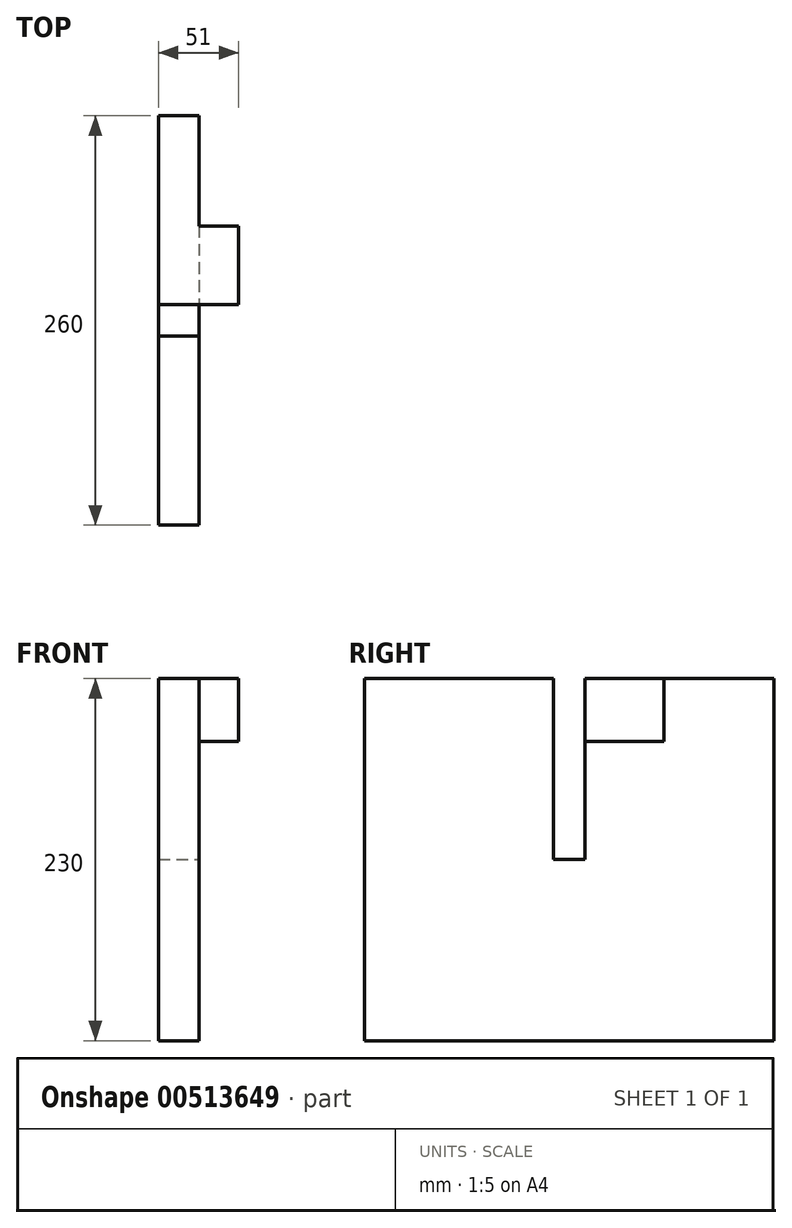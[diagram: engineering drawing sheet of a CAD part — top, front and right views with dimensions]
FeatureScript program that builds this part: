
annotation { "Feature Type Name" : "Feature", "Feature Type Description" : "" }
export const myFeature = defineFeature(function(context is Context, id is Id, definition is map)
    precondition{}
    {
        {
            var Q0;
            Q0=qCreatedBy(makeId("Right.planeOp"),FACE);
            var sketch = newSketch(context, id + "F0", { "sketchPlane" : qUnion([Q0])});
            skLineSegment(sketch, "E0.bottom", {"start": v(130, 115) * mm, "end": v(-130, 115) * mm});
            skLineSegment(sketch, "E0.top", {"start": v(130, -115) * mm, "end": v(-130, -115) * mm});
            skLineSegment(sketch, "E0.left", {"start": v(130, 115) * mm, "end": v(130, -115) * mm});
            skLineSegment(sketch, "E0.right", {"start": v(-130, 115) * mm, "end": v(-130, -115) * mm});
            skPoint(sketch, "E0.middle", {"position": v(0, 0) * mm});
            skSolve(sketch);
        }
        {
            var Q0;
            Q0=makeQuery(id+"F0.imprint","IMPRINT",FACE,{"disambiguationData":[TD([[makeQuery(id+"F0.imprint","IMPRINT",EDGE,{"derivedFrom":sQuery(id+"F0.wireOp",EDGE,"E0.bottom")}),1.0]])]});
            extrude(context, id + "F1", {"entities" : qUnion([Q0]), "depth" : 26 * mm});
        }
        {
            var Q0;
            Q0=makeQuery(id+"F1.opExtrude","CAP_FACE",FACE,{"disambiguationData":[OSD([sQuery(id+"F0.wireOp",EDGE,"E0.bottom"),sQuery(id+"F0.wireOp",EDGE,"E0.top"),sQuery(id+"F0.wireOp",EDGE,"E0.left"),sQuery(id+"F0.wireOp",EDGE,"E0.right")])],"isStart":false});
            var sketch = newSketch(context, id + "F2", { "sketchPlane" : qUnion([Q0])});
            skLineSegment(sketch, "E1.bottom", {"start": v(10, 115) * mm, "end": v(-10, 115) * mm});
            skLineSegment(sketch, "E1.top", {"start": v(10, -115) * mm, "end": v(-10, -115) * mm});
            skLineSegment(sketch, "E1.left", {"start": v(10, 115) * mm, "end": v(10, -115) * mm});
            skLineSegment(sketch, "E1.right", {"start": v(-10, 115) * mm, "end": v(-10, -115) * mm});
            skPoint(sketch, "E1.middle", {"position": v(0, 0) * mm});
            skLineSegment(sketch, "E2.bottom", {"start": v(-10, 0) * mm, "end": v(10, 0) * mm});
            skLineSegment(sketch, "E2.top", {"start": v(-10, -115) * mm, "end": v(10, -115) * mm});
            skLineSegment(sketch, "E2.left", {"start": v(-10, 0) * mm, "end": v(-10, -115) * mm});
            skLineSegment(sketch, "E2.right", {"start": v(10, 0) * mm, "end": v(10, -115) * mm});
            skSolve(sketch);
        }
        {
            var Q0;
            Q0=makeQuery(id+"F2.imprint","IMPRINT",FACE,{"disambiguationData":[TD([[makeQuery(id+"F2.imprint","IMPRINT",EDGE,{"derivedFrom":sQuery(id+"F2.wireOp",EDGE,"E1.bottom")}),1.0]])]});
            extrude(context, id + "F3", {"entities" : qUnion([Q0]), "operationType" : NewBodyOperationType.REMOVE, "oppositeDirection" : true, "depth" : 30 * mm});
        }
        {
            var Q0;
            {var subQ1=sQuery(id+"F0.wireOp",EDGE,"E0.left");var subQ3=sQuery(id+"F0.wireOp",EDGE,"E0.bottom");Q0=makeQuery(id+"F3.boolean.opBoolean","SPLIT",FACE,{"disambiguationData":[TD([makeQuery(id+"F1.opExtrude","SWEPT_FACE",FACE,{"disambiguationData":[OSD([subQ1])]})])],"derivedFrom":makeQuery(id+"F1.opExtrude","SWEPT_FACE",FACE,{"disambiguationData":[OSD([subQ3])]})});}
            var sketch = newSketch(context, id + "F4", { "sketchPlane" : qUnion([Q0])});
            skLineSegment(sketch, "E3.bottom", {"start": v(26, 10) * mm, "end": v(51, 10) * mm});
            skLineSegment(sketch, "E3.top", {"start": v(26, 60) * mm, "end": v(51, 60) * mm});
            skLineSegment(sketch, "E3.left", {"start": v(26, 10) * mm, "end": v(26, 60) * mm});
            skLineSegment(sketch, "E3.right", {"start": v(51, 10) * mm, "end": v(51, 60) * mm});
            skSolve(sketch);
        }
        {
            var Q0;
            Q0=makeQuery(id+"F4.imprint","IMPRINT",FACE,{"disambiguationData":[TD([[makeQuery(id+"F4.imprint","IMPRINT",EDGE,{"derivedFrom":sQuery(id+"F4.wireOp",EDGE,"E3.bottom")}),1.0]])]});
            extrude(context, id + "F5", {"entities" : qUnion([Q0]), "operationType" : NewBodyOperationType.ADD, "oppositeDirection" : true, "depth" : 40 * mm, "offsetDistance" : 25 * mm});
        }
    });
